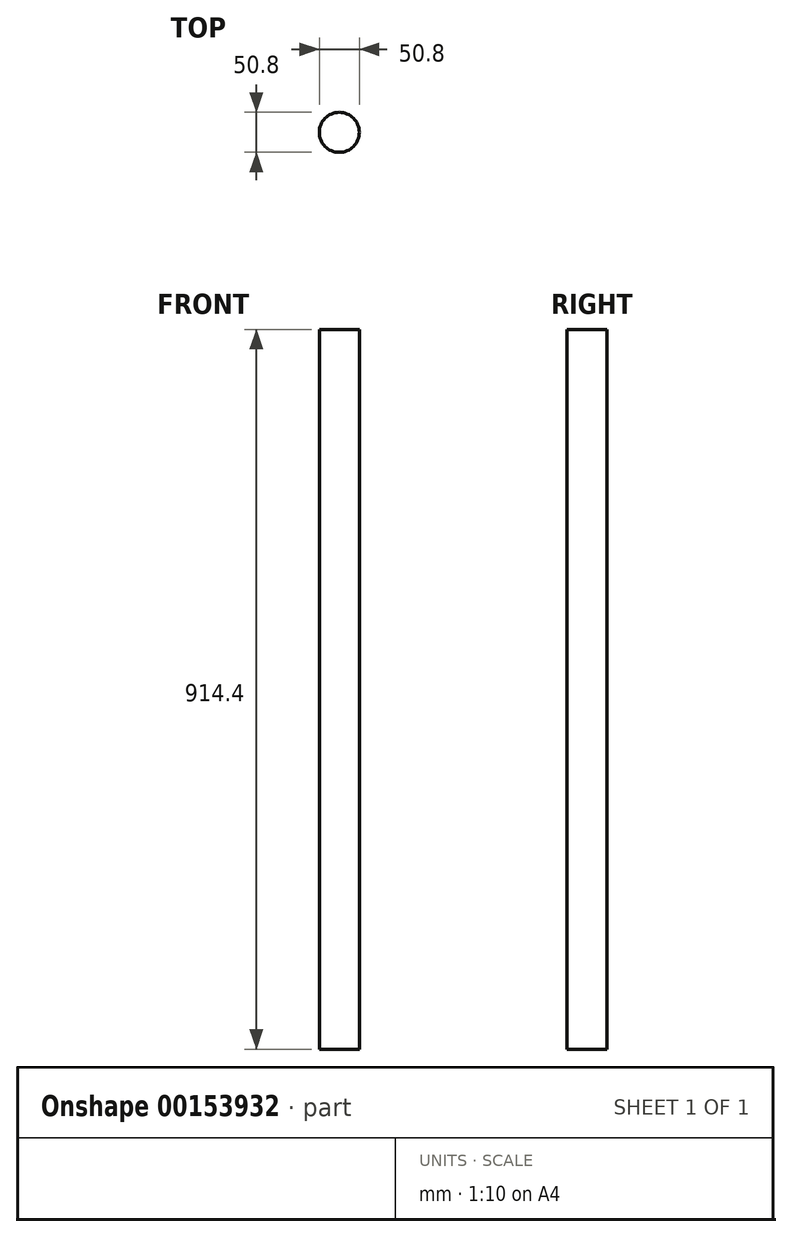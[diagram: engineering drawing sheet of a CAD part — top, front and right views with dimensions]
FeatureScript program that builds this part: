
annotation { "Feature Type Name" : "Feature", "Feature Type Description" : "" }
export const myFeature = defineFeature(function(context is Context, id is Id, definition is map)
    precondition{}
    {
        {
            var Q0;
            Q0=qCreatedBy(makeId("Top.planeOp"),FACE);
            var sketch = newSketch(context, id + "F0", { "sketchPlane" : qUnion([Q0])});
            skCircle(sketch, "E0", {"center": v(0, 0) * mm, "radius": 25.4 * mm});
            skSolve(sketch);
        }
        {
            var Q0;
            Q0 = qSketchRegion(id + "F0", true);
            extrude(context, id + "F1", {"entities" : qUnion([Q0]), "depth" : 304.8 * mm});
        }
        {
            var Q0;
            Q0 = qSketchRegion(id + "F0", true);
            extrude(context, id + "F2", {"entities" : qUnion([Q0]), "operationType" : NewBodyOperationType.ADD, "depth" : 914.4 * mm});
        }
    });
